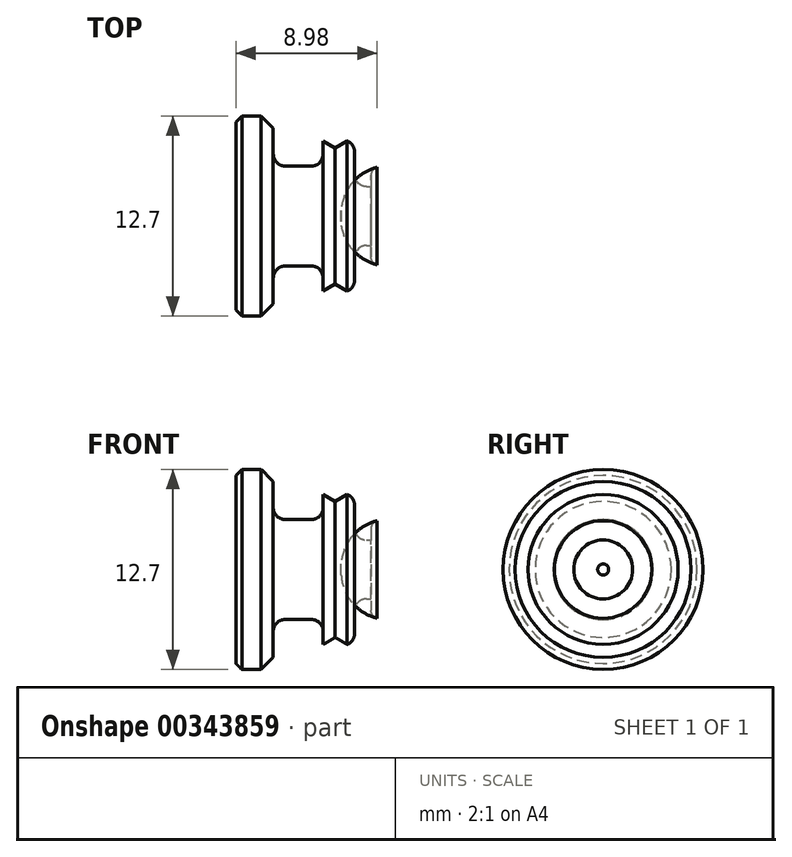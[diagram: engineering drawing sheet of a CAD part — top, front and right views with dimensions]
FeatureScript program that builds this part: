
annotation { "Feature Type Name" : "Feature", "Feature Type Description" : "" }
export const myFeature = defineFeature(function(context is Context, id is Id, definition is map)
    precondition{}
    {
        {
            var Q0;
            Q0=qCreatedBy(makeId("Front.planeOp"),FACE);
            var sketch = newSketch(context, id + "F0", { "sketchPlane" : qUnion([Q0])});
            skLineSegment(sketch, "E0", {"start": v(0, 0) * mm, "end": v(-12.7, 0) * mm});
            skLineSegment(sketch, "E1", {"start": v(-12.7, 0) * mm, "end": v(-12.7, 6.35) * mm});
            skLineSegment(sketch, "E2", {"start": v(-12.7, 6.35) * mm, "end": v(-10.33, 6.35) * mm});
            skLineSegment(sketch, "E3", {"start": v(-10.33, 6.35) * mm, "end": v(-10.33, 3.17) * mm});
            skLineSegment(sketch, "E4", {"start": v(-10.33, 3.17) * mm, "end": v(-7.15, 3.17) * mm});
            skLineSegment(sketch, "E5", {"start": v(-7.15, 3.17) * mm, "end": v(-7.15, 4.76) * mm});
            skLineSegment(sketch, "E6", {"start": v(-7.15, 4.76) * mm, "end": v(-6.39, 4.32) * mm});
            skLineSegment(sketch, "E7", {"start": v(-6.39, 4.32) * mm, "end": v(-5.63, 4.76) * mm});
            skLineSegment(sketch, "E8", {"start": v(-5.63, 4.76) * mm, "end": v(-5.16, 4.76) * mm});
            skLineSegment(sketch, "E9", {"start": v(-5.16, 4.76) * mm, "end": v(-5.16, 1.87) * mm});
            skArc(sketch, "E10", {"start": v(0, 0) * mm, "mid": v(-1.24, 2.61) * mm, "end": v(-4.1, 2.97) * mm});
            skLineSegment(sketch, "E11", {"start": v(-5.16, 1.87) * mm, "end": v(-4.1, 1.87) * mm});
            skLineSegment(sketch, "E12", {"start": v(-4.1, 2.97) * mm, "end": v(-4.1, 1.87) * mm});
            skPoint(sketch, "E13.start.orphan", {"position": v(-5.16, 3.18) * mm});
            skSolve(sketch);
        }
        {
            var Q0;
            Q0=makeQuery(id+"F0.imprint","IMPRINT",FACE,{"disambiguationData":[TD([[makeQuery(id+"F0.imprint","IMPRINT",EDGE,{"derivedFrom":sQuery(id+"F0.wireOp",EDGE,"E0")}),-1.0]])]});
            var Q1;
            Q1=sQuery(id+"F0.wireOp",EDGE,"E0");
            revolve(context, id + "F1", {"entities" : qUnion([Q0]), "axis" : qUnion([Q1]), "revolveType" : RevolveType.FULL});
        }
        {
            var Q0;
            Q0=makeQuery(id+"F1.opRevolve","SWEPT_EDGE",EDGE,{"disambiguationData":[OSD([sQuery(id+"F0.wireOp",EDGE,"E3"),sQuery(id+"F0.wireOp",EDGE,"E4")])]});
            var Q1;
            Q1=makeQuery(id+"F1.opRevolve","SWEPT_EDGE",EDGE,{"disambiguationData":[OSD([sQuery(id+"F0.wireOp",EDGE,"E4"),sQuery(id+"F0.wireOp",EDGE,"E5")])]});
            var Q2;
            Q2=makeQuery(id+"F1.opRevolve","SWEPT_EDGE",EDGE,{"disambiguationData":[OSD([sQuery(id+"F0.wireOp",EDGE,"E9"),sQuery(id+"F0.wireOp",EDGE,"E13")])]});
            fillet(context, id + "F2", {"entities" : qUnion([Q0, Q1, Q2]), "radius" : 0.76 * mm, "tangentPropagation" : true, "allowEdgeOverflow" : false});
        }
        {
            var Q0;
            Q0=makeQuery(id+"F1.opRevolve","SWEPT_EDGE",EDGE,{"disambiguationData":[OSD([sQuery(id+"F0.wireOp",EDGE,"E2"),sQuery(id+"F0.wireOp",EDGE,"E3")])]});
            chamfer(context, id + "F3", {"entities" : qUnion([Q0]), "width" : 0.76 * mm, "tangentPropagation" : true});
        }
        {
            var Q0;
            Q0=makeQuery(id+"F1.opRevolve","SWEPT_EDGE",EDGE,{"disambiguationData":[OSD([sQuery(id+"F0.wireOp",EDGE,"E1"),sQuery(id+"F0.wireOp",EDGE,"E2")])]});
            chamfer(context, id + "F4", {"entities" : qUnion([Q0]), "width" : 0.38 * mm, "tangentPropagation" : true});
        }
        {
            var Q0;
            Q0=makeQuery(id+"F1.opRevolve","SWEPT_EDGE",EDGE,{"disambiguationData":[OSD([sQuery(id+"F0.wireOp",EDGE,"E10"),sQuery(id+"F0.wireOp",EDGE,"E12")])]});
            fillet(context, id + "F5", {"entities" : qUnion([Q0]), "radius" : 0.5 * mm, "tangentPropagation" : true, "allowEdgeOverflow" : false});
        }
    });
